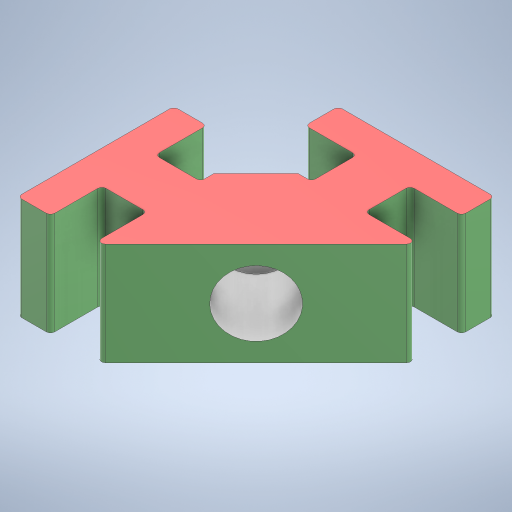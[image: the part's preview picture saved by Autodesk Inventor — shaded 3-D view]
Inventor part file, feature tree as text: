
AUTODESK INVENTOR PART (.ipt)
format: ipt  version: 2023 (Build 270158000, 158)  size: 296,960 bytes
history: native  units: mm
features: other x4, extrude x3, sketch x2, projected_geometry x1
ambient origin geometry x8: Origin, YZ Plane, XZ Plane, XY Plane, X Axis, Y Axis, Z Axis, Center Point
bodies: Body1 (feature_tree)
feature tree (10):
  other  "TmpPart3.ipt"
  sketch  "Sketch1"  dims[d0=10.0mm d1=3.2mm]
  extrude  "Extrusion1"  Depth=10.0mm
  extrude  "Extrusion2"  Depth=4.0mm TaperAngle=0.0deg
  extrude  "Extrusion3"  Depth=10.0mm TaperAngle=0.0deg
  other  "PLA2::TmpPart3.ipt"
  other  "TaggingFeature1"
  projected_geometry  "Projected Loop1"
  sketch  "Sketch2"  dims[d3=0.2mm d4=4.0mm d5=0.0mm d6=10.0mm d7=0.0mm d8=0.2mm d9=2.5mm d10=0.0mm]
  other  "PLA2"
